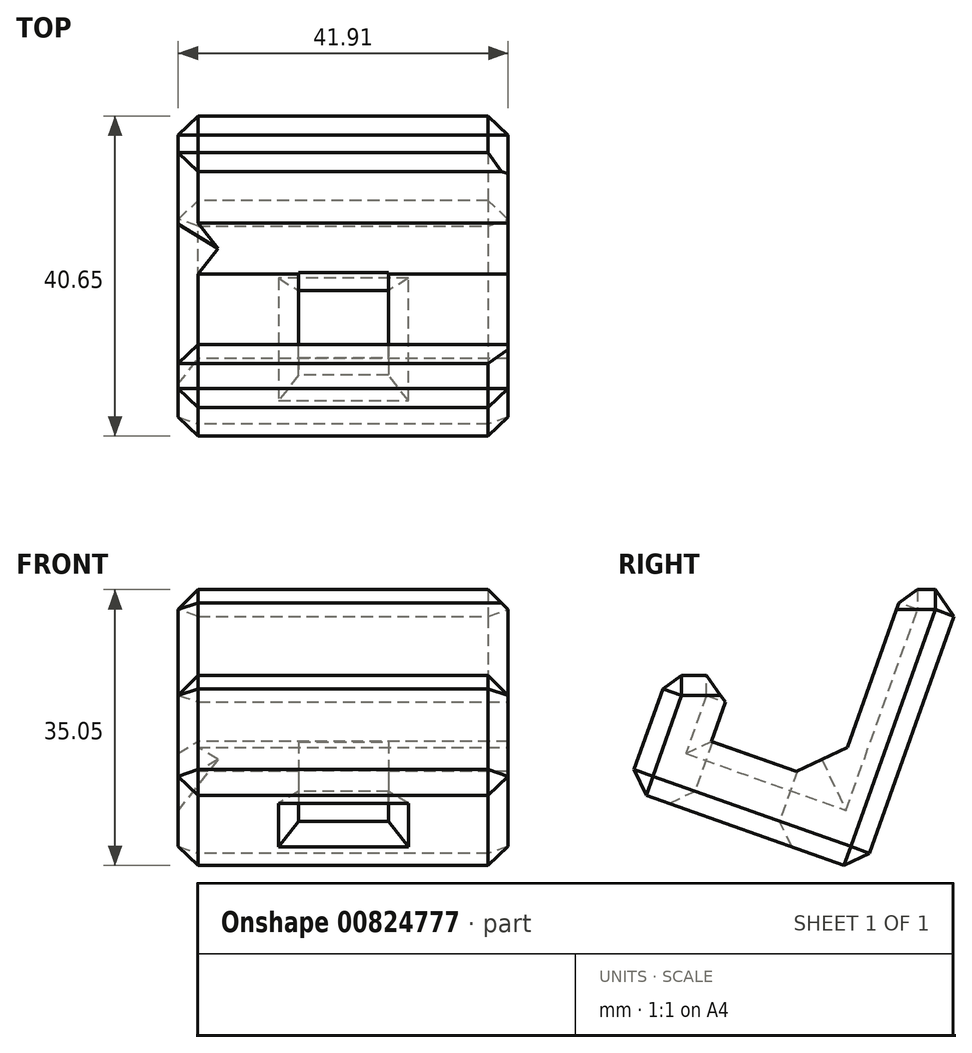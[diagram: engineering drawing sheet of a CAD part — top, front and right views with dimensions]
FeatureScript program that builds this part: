
annotation { "Feature Type Name" : "Feature", "Feature Type Description" : "" }
export const myFeature = defineFeature(function(context is Context, id is Id, definition is map)
    precondition{}
    {
        {
            var Q0;
            Q0=qCreatedBy(makeId("Right.planeOp"),FACE);
            var sketch = newSketch(context, id + "F0", { "sketchPlane" : qUnion([Q0])});
            skLineSegment(sketch, "E0", {"start": v(28.9, -0.02) * mm, "end": v(16.11, -35.92) * mm});
            skLineSegment(sketch, "E1", {"start": v(12.42, -24.83) * mm, "end": v(-3.14, -19.3) * mm});
            skLineSegment(sketch, "E2", {"start": v(-3.14, -19.3) * mm, "end": v(-0.16, -10.93) * mm});
            skLineSegment(sketch, "E3", {"start": v(16.11, -35.92) * mm, "end": v(-13.8, -25.3) * mm});
            skLineSegment(sketch, "E4", {"start": v(-13.8, -25.3) * mm, "end": v(-8.7, -10.93) * mm});
            skLineSegment(sketch, "E5", {"start": v(-8.7, -10.93) * mm, "end": v(-0.16, -10.93) * mm});
            skLineSegment(sketch, "E6", {"start": v(12.42, -24.83) * mm, "end": v(21.26, -0.02) * mm});
            skLineSegment(sketch, "E7", {"start": v(21.26, -0.02) * mm, "end": v(28.9, -0.02) * mm});
            skSolve(sketch);
        }
        {
            var Q0;
            Q0 = qSketchRegion(id + "F0", true);
            extrude(context, id + "F1", {"entities" : qUnion([Q0]), "depth" : 41.9 * mm, "offsetDistance" : 25.4 * mm});
        }
        {
            var Q0;
            Q0=makeQuery(id+"F1.opExtrude","SWEPT_FACE",FACE,{"disambiguationData":[OSD([sQuery(id+"F0.wireOp",EDGE,"E3")])]});
            var sketch = newSketch(context, id + "F2", { "sketchPlane" : qUnion([Q0])});
            skLineSegment(sketch, "E8.bottom", {"start": v(15.3, -3.65) * mm, "end": v(26.72, -3.65) * mm});
            skLineSegment(sketch, "E8.top", {"start": v(15.3, -15.08) * mm, "end": v(26.72, -15.08) * mm});
            skLineSegment(sketch, "E8.left", {"start": v(15.3, -3.65) * mm, "end": v(15.3, -15.08) * mm});
            skLineSegment(sketch, "E8.right", {"start": v(26.72, -3.65) * mm, "end": v(26.72, -15.08) * mm});
            skSolve(sketch);
        }
        {
            var Q0;
            Q0 = qSketchRegion(id + "F2", true);
            extrude(context, id + "F3", {"entities" : qUnion([Q0]), "operationType" : NewBodyOperationType.REMOVE, "oppositeDirection" : true, "depth" : 25.4 * mm, "offsetDistance" : 25.4 * mm});
        }
        {
            var Q0;
            Q0=makeQuery(id+"F1.opExtrude","CAP_FACE",FACE,{"disambiguationData":[OSD([sQuery(id+"F0.wireOp",EDGE,"E0"),sQuery(id+"F0.wireOp",EDGE,"E1"),sQuery(id+"F0.wireOp",EDGE,"E2"),sQuery(id+"F0.wireOp",EDGE,"E3"),sQuery(id+"F0.wireOp",EDGE,"E4"),sQuery(id+"F0.wireOp",EDGE,"E5"),sQuery(id+"F0.wireOp",EDGE,"E6"),sQuery(id+"F0.wireOp",EDGE,"E7")])],"isStart":true});
            var Q1;
            Q1=makeQuery(id+"F1.opExtrude","SWEPT_FACE",FACE,{"disambiguationData":[OSD([sQuery(id+"F0.wireOp",EDGE,"E7")])]});
            var Q2;
            Q2=makeQuery(id+"F1.opExtrude","SWEPT_FACE",FACE,{"disambiguationData":[OSD([sQuery(id+"F0.wireOp",EDGE,"E4")])]});
            var Q3;
            Q3=makeQuery(id+"F1.opExtrude","SWEPT_FACE",FACE,{"disambiguationData":[OSD([sQuery(id+"F0.wireOp",EDGE,"E5")])]});
            var Q4;
            Q4=makeQuery(id+"F1.opExtrude","SWEPT_FACE",FACE,{"disambiguationData":[OSD([sQuery(id+"F0.wireOp",EDGE,"E0")])]});
            var Q5;
            Q5=makeQuery(id+"F1.opExtrude","SWEPT_FACE",FACE,{"disambiguationData":[OSD([sQuery(id+"F0.wireOp",EDGE,"E3")])]});
            chamfer(context, id + "F4", {"entities" : qUnion([Q0, Q1, Q2, Q3, Q4, Q5]), "width" : 2.54 * mm, "tangentPropagation" : true});
        }
        {
            var Q0;
            Q0=makeQuery(id+"F1.opExtrude","SWEPT_EDGE",EDGE,{"disambiguationData":[OSD([sQuery(id+"F0.wireOp",EDGE,"E1"),sQuery(id+"F0.wireOp",EDGE,"E6")])]});
            chamfer(context, id + "F5", {"entities" : qUnion([Q0]), "width" : 5.08 * mm, "tangentPropagation" : true});
        }
    });
